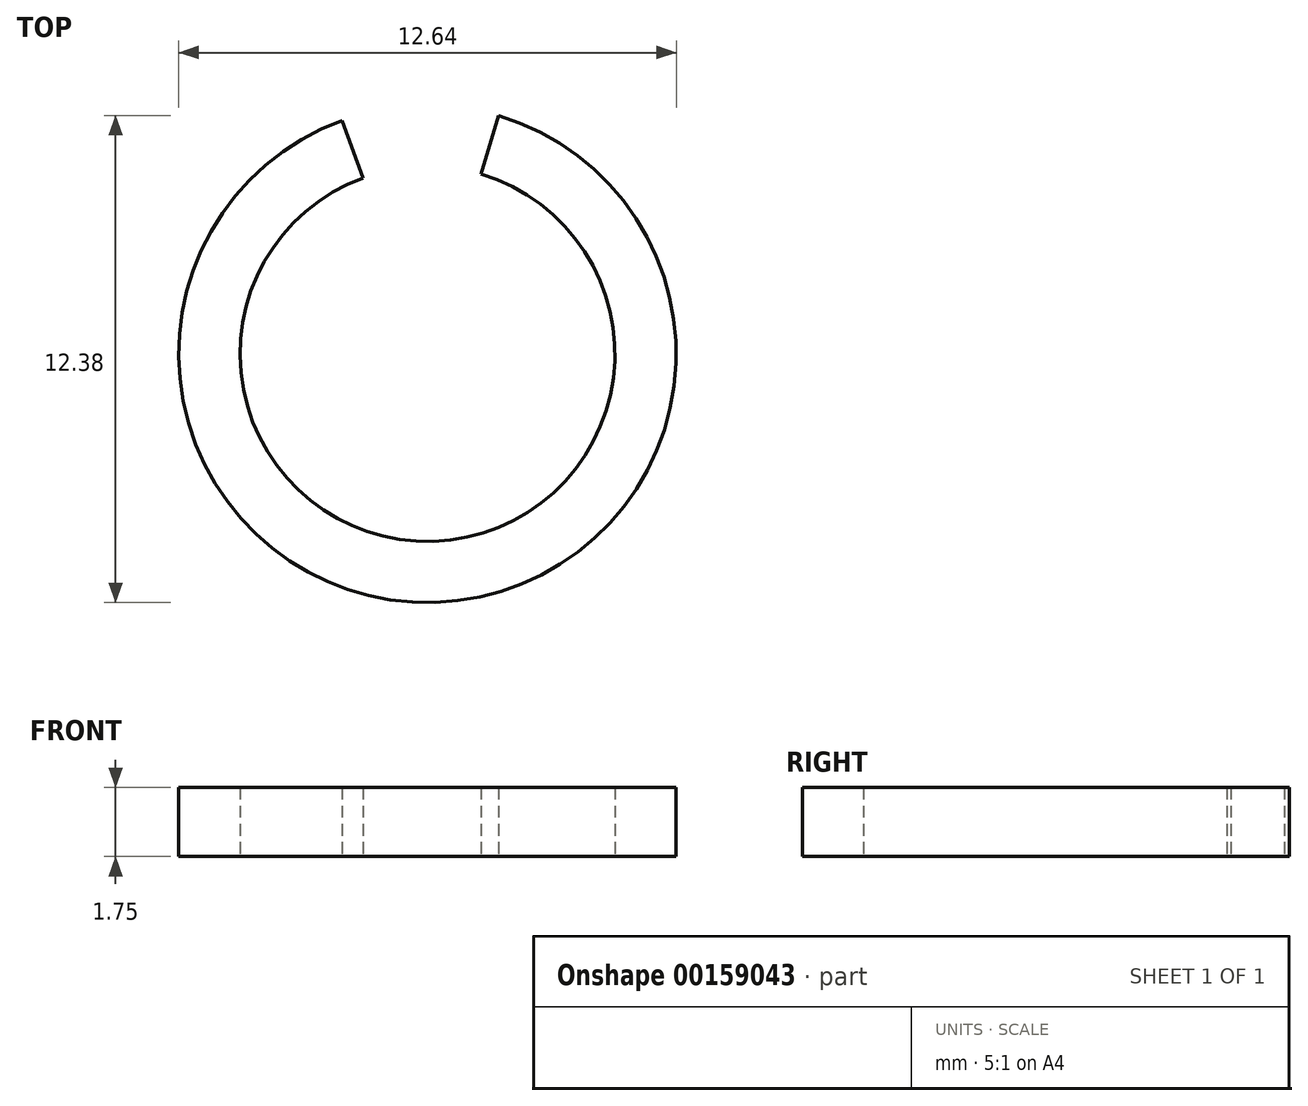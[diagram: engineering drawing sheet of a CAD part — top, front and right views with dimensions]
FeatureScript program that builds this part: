
annotation { "Feature Type Name" : "Feature", "Feature Type Description" : "" }
export const myFeature = defineFeature(function(context is Context, id is Id, definition is map)
    precondition{}
    {
        {
            var Q0;
            Q0=qCreatedBy(makeId("Top.planeOp"),FACE);
            var sketch = newSketch(context, id + "F0", { "sketchPlane" : qUnion([Q0])});
            skLineSegment(sketch, "E0", {"start": v(-1.64, 4.47) * mm, "end": v(-2.17, 5.93) * mm});
            skLineSegment(sketch, "E1", {"start": v(1.36, 4.57) * mm, "end": v(1.8, 6.06) * mm});
            skArc(sketch, "E2", {"start": v(-1.64, 4.47) * mm, "mid": v(0.15, -4.76) * mm, "end": v(1.36, 4.57) * mm});
            skArc(sketch, "E3", {"start": v(-2.17, 5.93) * mm, "mid": v(0.2, -6.32) * mm, "end": v(1.8, 6.06) * mm});
            skSolve(sketch);
        }
        {
            var Q0;
            Q0 = qSketchRegion(id + "F0", true);
            extrude(context, id + "F1", {"entities" : qUnion([Q0]), "depth" : 1.75 * mm});
        }
    });
